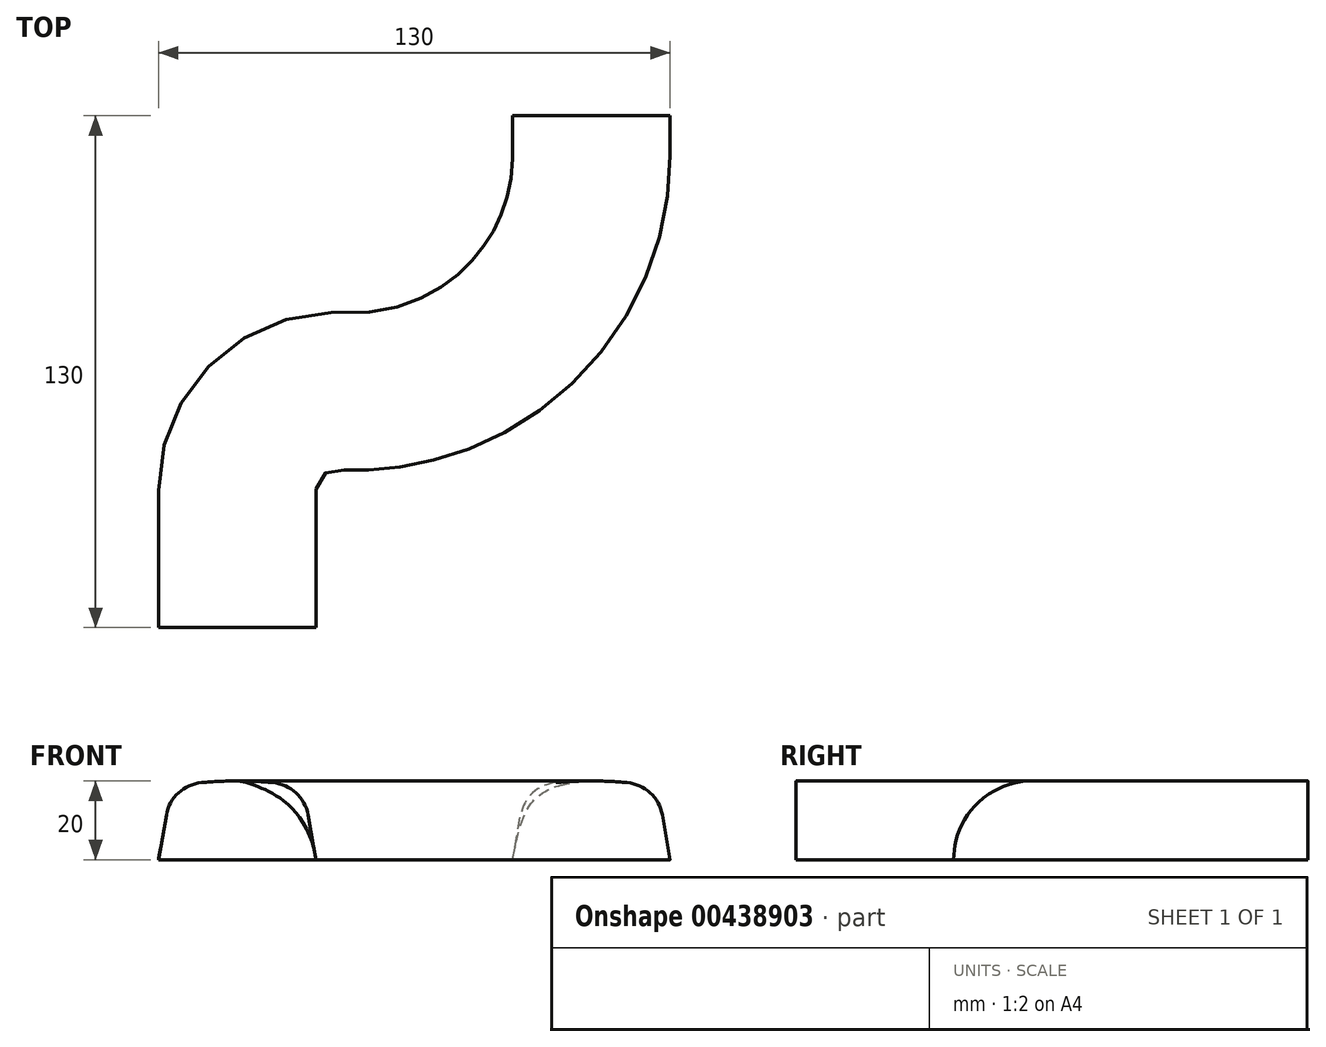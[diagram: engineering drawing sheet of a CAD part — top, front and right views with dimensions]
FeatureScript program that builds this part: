
annotation { "Feature Type Name" : "Feature", "Feature Type Description" : "" }
export const myFeature = defineFeature(function(context is Context, id is Id, definition is map)
    precondition{}
    {
        {
            var Q0;
            Q0=qCreatedBy(makeId("Top.planeOp"),FACE);
            var sketch = newSketch(context, id + "F0", { "sketchPlane" : qUnion([Q0])});
            skLineSegment(sketch, "E0", {"start": v(-30, -60) * mm, "end": v(-30, -25) * mm});
            skLineSegment(sketch, "E1", {"start": v(-5, 0) * mm, "end": v(0, 0) * mm});
            skLineSegment(sketch, "E2", {"start": v(60, 60) * mm, "end": v(60, 70) * mm});
            skPoint(sketch, "E3.visualSharp", {"position": v(-30, 0) * mm});
            skArc(sketch, "E3.filletArc", {"start": v(-5, 0) * mm, "mid": v(-22.68, -7.32) * mm, "end": v(-30, -25) * mm});
            skPoint(sketch, "E4.visualSharp", {"position": v(60, 0) * mm});
            skArc(sketch, "E4.filletArc", {"start": v(0, 0) * mm, "mid": v(42.43, 17.57) * mm, "end": v(60, 60) * mm});
            skSolve(sketch);
        }
        {
            var Q0;
            Q0=sQuery(id+"F0.wireOp",VERTEX,"E0.start");
            var Q1;
            Q1=sQuery(id+"F0.wireOp",EDGE,"E0");
            cPlane(context, id + "F1", {"entities" : qUnion([Q0, Q1]), "cplaneType" : CPlaneType.LINE_POINT, "offset" : 25 * mm, "width" : 150 * mm, "height" : 150 * mm});
        }
        {
            var Q0;
            Q0=qCreatedBy(id+"F1.planeOp",FACE);
            var sketch = newSketch(context, id + "F2", { "sketchPlane" : qUnion([Q0])});
            skLineSegment(sketch, "E5", {"start": v(30, 0) * mm, "end": v(30, -20) * mm, "construction": true});
            skLineSegment(sketch, "E6.bottom", {"start": v(50, 0) * mm, "end": v(10, 0) * mm, "construction": true});
            skLineSegment(sketch, "E6.top", {"start": v(50, -20) * mm, "end": v(10, -20) * mm, "construction": true});
            skLineSegment(sketch, "E6.left", {"start": v(50, 0) * mm, "end": v(50, -20) * mm, "construction": true});
            skLineSegment(sketch, "E6.right", {"start": v(10, 0) * mm, "end": v(10, -20) * mm, "construction": true});
            skLineSegment(sketch, "E7", {"start": v(50, -20) * mm, "end": v(48, -8.63) * mm});
            skLineSegment(sketch, "E8.MirrorCS", {"start": v(10, -20) * mm, "end": v(12, -8.63) * mm});
            skArc(sketch, "E9", {"start": v(39.05, -0.41) * mm, "mid": v(30, 0) * mm, "end": v(20.95, -0.41) * mm});
            skPoint(sketch, "E10.visualSharp", {"position": v(46.72, -1.4) * mm});
            skArc(sketch, "E10.filletArc", {"start": v(48, -8.63) * mm, "mid": v(44.92, -3) * mm, "end": v(39.05, -0.41) * mm});
            skPoint(sketch, "E11.visualSharp", {"position": v(13.28, -1.4) * mm});
            skArc(sketch, "E11.filletArc", {"start": v(20.95, -0.41) * mm, "mid": v(15.08, -3) * mm, "end": v(12, -8.63) * mm});
            skSolve(sketch);
        }
        {
            var Q0;
            Q0=sQuery(id+"F0.wireOp",VERTEX,"E2.end");
            var Q1;
            Q1=sQuery(id+"F0.wireOp",EDGE,"E2");
            cPlane(context, id + "F3", {"entities" : qUnion([Q0, Q1]), "cplaneType" : CPlaneType.LINE_POINT, "offset" : 25 * mm, "width" : 150 * mm, "height" : 150 * mm});
        }
        {
            var Q0;
            Q0=qCreatedBy(id+"F3.planeOp",FACE);
            var sketch = newSketch(context, id + "F4", { "sketchPlane" : qUnion([Q0])});
            skLineSegment(sketch, "E12", {"start": v(-60, 0) * mm, "end": v(-60, -20) * mm, "construction": true});
            skLineSegment(sketch, "E13.bottom", {"start": v(-80, -20) * mm, "end": v(-40, -20) * mm, "construction": true});
            skLineSegment(sketch, "E13.top", {"start": v(-80, 0) * mm, "end": v(-40, 0) * mm, "construction": true});
            skLineSegment(sketch, "E13.left", {"start": v(-80, -20) * mm, "end": v(-80, 0) * mm, "construction": true});
            skLineSegment(sketch, "E13.right", {"start": v(-40, -20) * mm, "end": v(-40, 0) * mm, "construction": true});
            skLineSegment(sketch, "E14", {"start": v(-80, -20) * mm, "end": v(-78, -8.63) * mm});
            skLineSegment(sketch, "E15.MirrorCS", {"start": v(-40, -20) * mm, "end": v(-42, -8.63) * mm});
            skArc(sketch, "E16", {"start": v(-50.95, -0.41) * mm, "mid": v(-60, 0) * mm, "end": v(-69.05, -0.41) * mm});
            skPoint(sketch, "E17.visualSharp", {"position": v(-43.28, -1.4) * mm});
            skArc(sketch, "E17.filletArc", {"start": v(-42, -8.63) * mm, "mid": v(-45.08, -3) * mm, "end": v(-50.95, -0.41) * mm});
            skPoint(sketch, "E18.visualSharp", {"position": v(-76.72, -1.4) * mm});
            skArc(sketch, "E18.filletArc", {"start": v(-69.05, -0.41) * mm, "mid": v(-74.92, -3) * mm, "end": v(-78, -8.63) * mm});
            skSolve(sketch);
        }
        {
            var Q0;
            Q0=qCreatedBy(makeId("Right.planeOp"),FACE);
            var sketch = newSketch(context, id + "F5", { "sketchPlane" : qUnion([Q0])});
            skArc(sketch, "E19", {"start": v(-20, -20) * mm, "mid": v(0, 0) * mm, "end": v(20, -20) * mm});
            skLineSegment(sketch, "E20", {"start": v(20, -20) * mm, "end": v(-20, -20) * mm, "construction": true});
            skSolve(sketch);
        }
        {
            var Q0;
            Q0=qCreatedBy(makeId("Top.planeOp"),FACE);
            cPlane(context, id + "F6", {"entities" : qUnion([Q0]), "cplaneType" : CPlaneType.OFFSET, "offset" : 20 * mm, "oppositeDirection" : true, "width" : 150 * mm, "height" : 150 * mm});
        }
        {
            var Q0;
            Q0=qCreatedBy(id+"F6.planeOp",FACE);
            var sketch = newSketch(context, id + "F7", { "sketchPlane" : qUnion([Q0])});
            skLineSegment(sketch, "E21.0", {"start": v(80, 60) * mm, "end": v(80, 70) * mm});
            skLineSegment(sketch, "E21.1", {"start": v(-10, -60) * mm, "end": v(-10, -25) * mm});
            skArc(sketch, "E21.2", {"start": v(-5, -20) * mm, "mid": v(-8.54, -21.46) * mm, "end": v(-10, -25) * mm});
            skLineSegment(sketch, "E21.3", {"start": v(-5, -20) * mm, "end": v(0, -20) * mm});
            skArc(sketch, "E21.4", {"start": v(0, -20) * mm, "mid": v(56.57, 3.43) * mm, "end": v(80, 60) * mm});
            skSolve(sketch);
        }
        {
            var Q0;
            Q0=qCreatedBy(id+"F6.planeOp",FACE);
            var sketch = newSketch(context, id + "F8", { "sketchPlane" : qUnion([Q0])});
            skLineSegment(sketch, "E22.0", {"start": v(40, 60) * mm, "end": v(40, 70) * mm});
            skLineSegment(sketch, "E22.1", {"start": v(-50, -60) * mm, "end": v(-50, -25) * mm});
            skArc(sketch, "E22.2", {"start": v(-5, 20) * mm, "mid": v(-36.82, 6.82) * mm, "end": v(-50, -25) * mm});
            skLineSegment(sketch, "E22.3", {"start": v(-5, 20) * mm, "end": v(0, 20) * mm});
            skArc(sketch, "E22.4", {"start": v(0, 20) * mm, "mid": v(28.28, 31.72) * mm, "end": v(40, 60) * mm});
            skSolve(sketch);
        }
        {
            var Q0;
            Q0 = qSketchRegion(id + "F2", true);
            var Q1;
            Q1 = qSketchRegion(id + "F5", true);
            var Q2;
            Q2 = qSketchRegion(id + "F4", true);
            var Q3;
            Q3 = qConstructionFilter(qBodyType(qCreatedBy(id + "F2" ,EDGE), BodyType.WIRE), ConstructionObject.NO);
            var Q4;
            Q4 = qConstructionFilter(qBodyType(qCreatedBy(id + "F5" ,EDGE), BodyType.WIRE), ConstructionObject.NO);
            var Q5;
            Q5 = qConstructionFilter(qBodyType(qCreatedBy(id + "F4" ,EDGE), BodyType.WIRE), ConstructionObject.NO);
            var Q6;
            Q6 = qConstructionFilter(qBodyType(qCreatedBy(id + "F0" ,EDGE), BodyType.WIRE), ConstructionObject.NO);
            var Q7;
            Q7 = qConstructionFilter(qBodyType(qCreatedBy(id + "F7" ,EDGE), BodyType.WIRE), ConstructionObject.NO);
            var Q8;
            Q8 = qConstructionFilter(qBodyType(qCreatedBy(id + "F8" ,EDGE), BodyType.WIRE), ConstructionObject.NO);
            loft(context, id + "F9", {"bodyType" : ToolBodyType.SURFACE, "addGuides" : true, "sheetProfilesArray" : [{ "sheetProfileEntities" : qUnion([Q0]) }, { "sheetProfileEntities" : qUnion([Q1]) }, { "sheetProfileEntities" : qUnion([Q2]) }], "wireProfilesArray" : [{ "wireProfileEntities" : qUnion([Q3]) }, { "wireProfileEntities" : qUnion([Q4]) }, { "wireProfileEntities" : qUnion([Q5]) }], "guidesArray" : [{ "guideEntities" : qUnion([Q6]), "guideDerivativeType" : LoftGuideDerivativeType.DEFAULT, "guideDerivativeMagnitude" : 1 }, { "guideEntities" : qUnion([Q7]), "guideDerivativeType" : LoftGuideDerivativeType.DEFAULT, "guideDerivativeMagnitude" : 1 }, { "guideEntities" : qUnion([Q8]), "guideDerivativeType" : LoftGuideDerivativeType.DEFAULT, "guideDerivativeMagnitude" : 1 }]});
        }
    });
